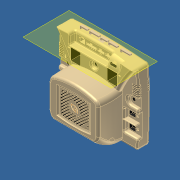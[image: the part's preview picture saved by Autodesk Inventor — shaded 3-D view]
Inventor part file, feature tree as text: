
AUTODESK INVENTOR PART (.ipt)
format: ipt  version: 2012 (Build 160160000, 160)  size: 3,485,696 bytes
history: native  units: in
note: dims shown in document units (in); Inventor stores cm internally (conversion verified against a paired STEP export)
features: sketch x47, extrude x43, fillet x43, projected_geometry x20, plane x6, hole x1, revolve x1, emboss x1
ambient origin geometry x8: Origin, YZ Plane, XZ Plane, XY Plane, X Axis, Y Axis, Z Axis, Center Point
bodies: Solid1 (feature_tree)
feature tree (162):
  extrude  "Extrusion3"  Depth=4.251in
  extrude  "Extrusion4"  Depth=0.0535in
  extrude  "Extrusion5"  Depth=0.72in
  extrude  "Extrusion6"  Depth=1.308in TaperAngle=0.0deg
  extrude  "Extrusion7"  Depth=0.052in
  extrude  "Extrusion9"  Depth=0.052in
  extrude  "Extrusion10"  Depth=1.308in TaperAngle=0.0deg
  extrude  "Extrusion11"  Depth=1.308in TaperAngle=0.0deg
  extrude  "Extrusion12"  Depth=0.218in TaperAngle=0.0deg
  extrude  "Extrusion13"  Depth=2.01in
  fillet  "Fillet1"  Radius=0.768in
  fillet  "Fillet3"  Radius=0.31in
  fillet  "Fillet4"  Radius=0.615in
  fillet  "Fillet5"  Radius=0.125in
  fillet  "Fillet6"  Radius=0.081in
  fillet  "Fillet7"  Radius=0.05in
  fillet  "Fillet8"  Radius=0.05in
  extrude  "Extrusion15"  Depth=0.036in
  fillet  "Fillet9"  Radius=0.05in
  fillet  "Fillet10"  Radius=0.4706in
  fillet  "Fillet11"  Radius=0.4706in
  fillet  "Fillet12"  Radius=0.218in
  fillet  "Fillet13"  Radius=0.15in
  fillet  "Fillet14"  Radius=0.15in
  fillet  "Fillet15"  Radius=0.15in
  plane  "Work Plane1"
  extrude  "Extrusion16"  Depth=0.15in
  fillet  "Fillet17"  Radius=0.15in
  fillet  "Fillet18"  Radius=0.15in
  fillet  "Fillet19"  [1 undecoded]
  fillet  "Fillet20"  Radius=5.0in
  fillet  "Fillet21"  Radius=0.3in
  fillet  "Fillet22"  Radius=0.3in
  fillet  "Fillet23"  Radius=0.272in
  extrude  "Extrusion17"  Depth=0.125in
  fillet  "Fillet24"  Radius=0.096in
  extrude  "Extrusion18"  Depth=0.054in TaperAngle=0.0deg
  extrude  "Extrusion19"  Depth=0.055in
  extrude  "Extrusion20"  Depth=0.055in
  plane  "Work Plane2"
  extrude  "Extrusion21"  Depth=0.055in
  extrude  "Extrusion22"  TaperAngle=90.0deg  [1 undecoded]
  fillet  "Fillet25"  Radius=0.05in
  extrude  "Extrusion23"  Depth=0.05in
  extrude  "Extrusion24"  Depth=0.05in
  extrude  "Extrusion25"  Depth=0.055in
  fillet  "Fillet26"  Radius=0.05in
  plane  "Work Plane3"
  extrude  "Extrusion26"  Depth=0.055in
  fillet  "Fillet27"  Radius=0.05in
  hole  "Hole1"  [1 undecoded]
  extrude  "Extrusion27"  Depth=0.05in
  fillet  "Fillet28"  Radius=0.055in
  fillet  "Fillet29"  [1 undecoded]
  fillet  "Fillet30"  [1 undecoded]
  fillet  "Fillet31"  [1 undecoded]
  fillet  "Fillet32"  Radius=0.05in
  fillet  "Fillet33"  Radius=0.055in
  fillet  "Fillet34"  Radius=0.055in
  fillet  "Fillet35"  Radius=0.055in
  plane  "Work Plane4"
  extrude  "Extrusion28"  TaperAngle=90.0deg  [1 undecoded]
  fillet  "Fillet36"  Radius=0.05in
  extrude  "Extrusion29"  TaperAngle=90.0deg  [1 undecoded]
  extrude  "Extrusion30"  Depth=0.055in
  extrude  "Extrusion31"  Depth=0.05in
  extrude  "Extrusion32"  TaperAngle=90.0deg  [1 undecoded]
  extrude  "Extrusion33"  TaperAngle=90.0deg  [1 undecoded]
  extrude  "Extrusion34"  Depth=0.055in
  revolve  "Revolution1"  [1 undecoded]
  extrude  "Extrusion35"  Depth=0.05in
  extrude  "Extrusion36"  Depth=0.08in
  plane  "Work Plane5"
  emboss  "Emboss1"
  sketch  "Sketch38"  dims[d135=0.615in d138=0.524in]
  extrude  "Extrusion39"  Depth=0.84in TaperAngle=0.0deg
  fillet  "Fillet38"  Radius=0.524in
  plane  "Work Plane9"
  extrude  "Extrusion40"  Depth=0.524in
  extrude  "Extrusion41"  Depth=0.647in TaperAngle=0.0deg
  fillet  "Fillet39"  Radius=0.22in
  extrude  "Extrusion42"  Depth=0.219in
  extrude  "Extrusion43"  Depth=0.1in
  fillet  "Fillet40"  Radius=0.058in
  extrude  "Extrusion44"  Depth=0.056in
  extrude  "Extrusion45"  Depth=0.1in
  fillet  "Fillet41"  Radius=0.1in
  extrude  "Extrusion46"  Depth=0.13in
  extrude  "Extrusion47"  Depth=0.357in
  fillet  "Fillet42"  Radius=0.334in
  extrude  "Extrusion48"  Depth=1.1875in
  extrude  "Extrusion49"  Depth=0.344in
  fillet  "Fillet43"  Radius=0.489in
  fillet  "Fillet44"  Radius=0.337in
  fillet  "Fillet45"  Radius=0.25in
  fillet  "Fillet46"  Radius=0.143in
  sketch  "Sketch1"  dims[d0=3.876in d1=4.251in]
  sketch  "Sketch2"  dims[d5=0.0535in d6=0.0535in]
  sketch  "Sketch3"  dims[d9=2.005in d10=0.0in d11=0.72in]
  sketch  "Sketch4"  dims[d12=0.72in d13=1.308in d14=0.0in]
  sketch  "Sketch5"  dims[d15=0.052in d16=0.052in]
  sketch  "Sketch6"  dims[d17=0.052in d18=0.052in]
  sketch  "Sketch7"  dims[d19=2.475in d20=0.0in d21=1.308in d22=0.0in]
  sketch  "Sketch8"  dims[d23=1.308in d24=0.0in d27=1.308in d28=0.0in]
  sketch  "Sketch9"  dims[d29=1.308in d30=0.0in d31=0.218in d32=0.0in]
  sketch  "Sketch10"  dims[d34=0.543in d35=2.01in d36=0.768in d37=0.31in d38=0.0in d39=0.615in d40=0.0in d41=0.125in d43=0.081in d44=0.05in d45=0.05in]
  sketch  "Sketch11"  dims[d46=0.05in d47=0.036in d48=0.05in d51=0.4706in d52=0.4706in d53=0.218in d54=0.0in d55=0.15in d56=0.15in d57=0.15in]
  sketch  "Sketch12"  dims[d58=0.078in d59=0.15in d60=0.15in d61=0.15in d62=-0.6875in d63=5.0in d64=0.0in d66=0.3in d67=0.3in d68=0.272in]
  sketch  "Sketch13"  dims[d69=0.409in d70=0.125in d71=0.096in]
  sketch  "Sketch14"  dims[d72=0.125in d74=0.054in d75=0.0in]
  sketch  "Sketch15"  dims[d76=0.125in d77=0.055in]
  sketch  "Sketch16"  dims[d78=0.055in d79=0.055in]
  sketch  "Sketch17"  dims[d80=0.055in d81=0.055in]
  sketch  "Sketch18"  dims[d82=90.0deg d83=90.0deg d84=0.05in]
  sketch  "Sketch19"  dims[d85=0.05in d86=0.05in]
  projected_geometry  "Projected Loop1"
  sketch  "Sketch20"  dims[d88=0.05in d89=0.05in]
  sketch  "Sketch21"  dims[d90=0.055in d91=0.055in d92=0.05in]
  sketch  "Sketch22"  dims[d93=0.05in d94=0.055in d95=0.05in]
  projected_geometry  "Projected Loop2"
  projected_geometry  "Projected Loop3"
  projected_geometry  "Projected Loop4"
  projected_geometry  "Projected Loop5"
  projected_geometry  "Projected Loop6"
  projected_geometry  "Projected Loop7"
  projected_geometry  "Projected Loop8"
  projected_geometry  "Projected Loop9"
  sketch  "Sketch23"  dims[d96=0.055in d97=90.0deg]
  sketch  "Sketch24"  dims[d98=90.0deg d99=0.05in d100=0.055in d101=90.0deg d102=90.0deg d103=90.0deg d104=0.05in d105=0.055in d106=0.055in d107=0.055in]
  projected_geometry  "Projected Loop10"
  projected_geometry  "Projected Loop11"
  sketch  "Sketch26"  dims[d108=0.05in d109=90.0deg d110=0.05in]
  projected_geometry  "Projected Loop19"
  projected_geometry  "Projected Loop20"
  projected_geometry  "Projected Loop21"
  projected_geometry  "Projected Loop22"
  projected_geometry  "Projected Loop23"
  projected_geometry  "Projected Loop24"
  projected_geometry  "Projected Loop25"
  sketch  "Sketch27"  dims[d111=0.055in d112=90.0deg]
  sketch  "Sketch28"  dims[d113=0.05in d114=0.055in]
  sketch  "Sketch29"  dims[d115=0.055in d116=0.05in]
  sketch  "Sketch30"  dims[d117=0.05in d118=90.0deg]
  sketch  "Sketch31"  dims[d119=90.0deg d120=90.0deg]
  projected_geometry  "Projected Loop26"
  sketch  "Sketch32"  dims[d121=0.05in d123=0.055in]
  sketch  "Sketch33"  dims[d124=90.0deg d125=0.055in]
  sketch  "Sketch34"  dims[d126=0.05in d127=0.05in]
  sketch  "Sketch35"  dims[d128=0.055in d129=0.08in]
  projected_geometry  "Projected Loop27"
  sketch  "Sketch36"  dims[d130=0.08in d131=0.84in d132=0.0in d134=0.524in]
  sketch  "Sketch39"  dims[d139=0.615in d140=0.647in d141=0.0in d142=0.22in]
  sketch  "Sketch40"  dims[d143=0.255in d144=0.219in]
  sketch  "Sketch41"  dims[d145=0.083in d146=0.1in d147=0.058in]
  sketch  "Sketch42"  dims[d148=0.549in d149=0.056in]
  sketch  "Sketch43"  dims[d150=0.056in d151=0.1in d152=0.1in]
  sketch  "Sketch44"  dims[d153=0.13in d154=0.13in]
  sketch  "Sketch45"  dims[d155=0.13in d156=0.357in d157=0.334in]
  sketch  "Sketch46"  dims[d158=0.248in d159=0.0in d160=1.1875in]
  sketch  "Sketch47"  dims[d161=0.114in d162=0.344in d163=0.489in d164=0.0in d165=0.337in d166=0.25in d167=0.143in d168=0.0in]
  sketch  "Sketch48"  dims[d169=0.066in]
  sketch  "Sketch49"  dims[d170=0.431in d171=0.51in d172=0.51in d173=0.068in d174=0.067in d175=0.067in d176=0.234in d177=0.0in d178=0.282in d179=0.422in d180=0.446in d181=0.167in d182=0.0in d183=0.141in d184=0.04in d185=0.04in d186=0.04in d187=0.04in d190=0.04in d191=0.04in d192=0.04in d193=0.062in d194=0.0in d195=0.0in d196=0.0in d197=0.04in d198=0.04in d199=0.04in d200=0.04in d201=0.0in d202=0.0in d203=0.04in d204=0.04in d205=0.0in d206=7.0in d207=0.0in d208=0.02in d209=3.4375in d210=0.17in d211=0.17in d212=0.5in d213=0.0in d214=0.02in d215=0.174in d216=0.5in d217=0.375in d218=0.25in d219=0.5635in d220=0.745in d221=0.8108in d222=0.618in d223=0.234in d224=0.0in d225=0.08in d226=0.08in d227=0.08in d228=0.08in d229=0.08in d230=0.08in d231=0.035in d232=0.035in d233=0.068in d234=0.51in d235=0.067in d236=0.067in d237=0.51in d238=0.618in d239=0.446in d240=0.141in d241=0.04in d243=0.04in d245=0.04in d246=0.04in d247=0.04in d248=0.062in d249=0.0in d250=0.0in d251=0.04in d252=0.04in d253=0.0in d254=0.04in d255=0.04in d256=0.0in d257=0.04in d258=0.04in d259=0.0in d261=0.04in d262=0.0in d263=0.04in d264=-1.4375in d265=0.167in d266=0.167in d267=0.5in d268=0.0in d269=0.02in d270=0.0001in d271=0.0in d272=0.0001in d273=0.0in d274=0.055in d275=0.207in d276=0.3in d277=0.0in d278=0.0001in d279=0.0in d280=0.34in d281=0.335in d282=0.123in d283=0.34in d284=0.335in d285=0.123in d286=0.068in d287=0.068in d288=0.161in d289=0.0in d290=0.335in d291=0.335in d292=0.34in d293=0.34in d294=0.068in d295=0.068in d296=0.123in d297=0.123in d298=0.0in d299=0.0in d300=90.0deg d301=0.066in d302=0.066in d303=0.033in d304=0.033in d305=0.033in d306=0.066in d307=0.066in d308=0.066in d309=0.066in d310=0.05in d311=0.05in d312=0.05in d313=0.0in d314=0.01in d315=0.01in d316=0.01in d317=0.033in d318=0.033in d319=0.033in d320=0.033in d321=0.033in d322=0.033in d323=0.0001in d324=0.0in d325=3.9375in d335=0.0001in d336=0.0in d338=0.2in d340=0.03in d341=0.03in d342=0.03in d346=0.01in d347=0.0in d351=0.03in d352=0.03in d354=0.01in d355=3.875in d356=0.07in d357=0.106in d358=0.07in d359=0.106in d360=0.534in d361=0.07in d362=0.106in d363=0.4in d364=0.07in d365=0.106in d366=0.294in d367=0.07in d368=0.106in d369=0.546in d370=0.136in d371=0.0in d372=0.07in d373=0.315in d374=0.0in d375=0.035in d376=0.07in d377=0.511in d378=0.28in d379=0.0in d380=0.07in d381=0.453in d382=0.0in d383=0.035in d384=0.07in d385=0.43in d386=0.27in d387=0.0in d388=0.07in d389=0.345in d390=0.0in d391=0.035in d392=0.07in d393=0.358in d394=0.27in d395=0.0in d396=0.07in d397=0.4in d398=0.0in d399=0.035in d400=0.07in d401=0.555in d402=0.25in d403=0.0in d404=0.07in d405=0.473in d406=0.0in d407=0.035in d408=0.035in d409=0.035in d410=0.01in]
note: 11 required parameter values undecoded (feature->parameter linkage not recoverable at this tier; creation-order binding heuristic only, values carry confidence <= 0.55)